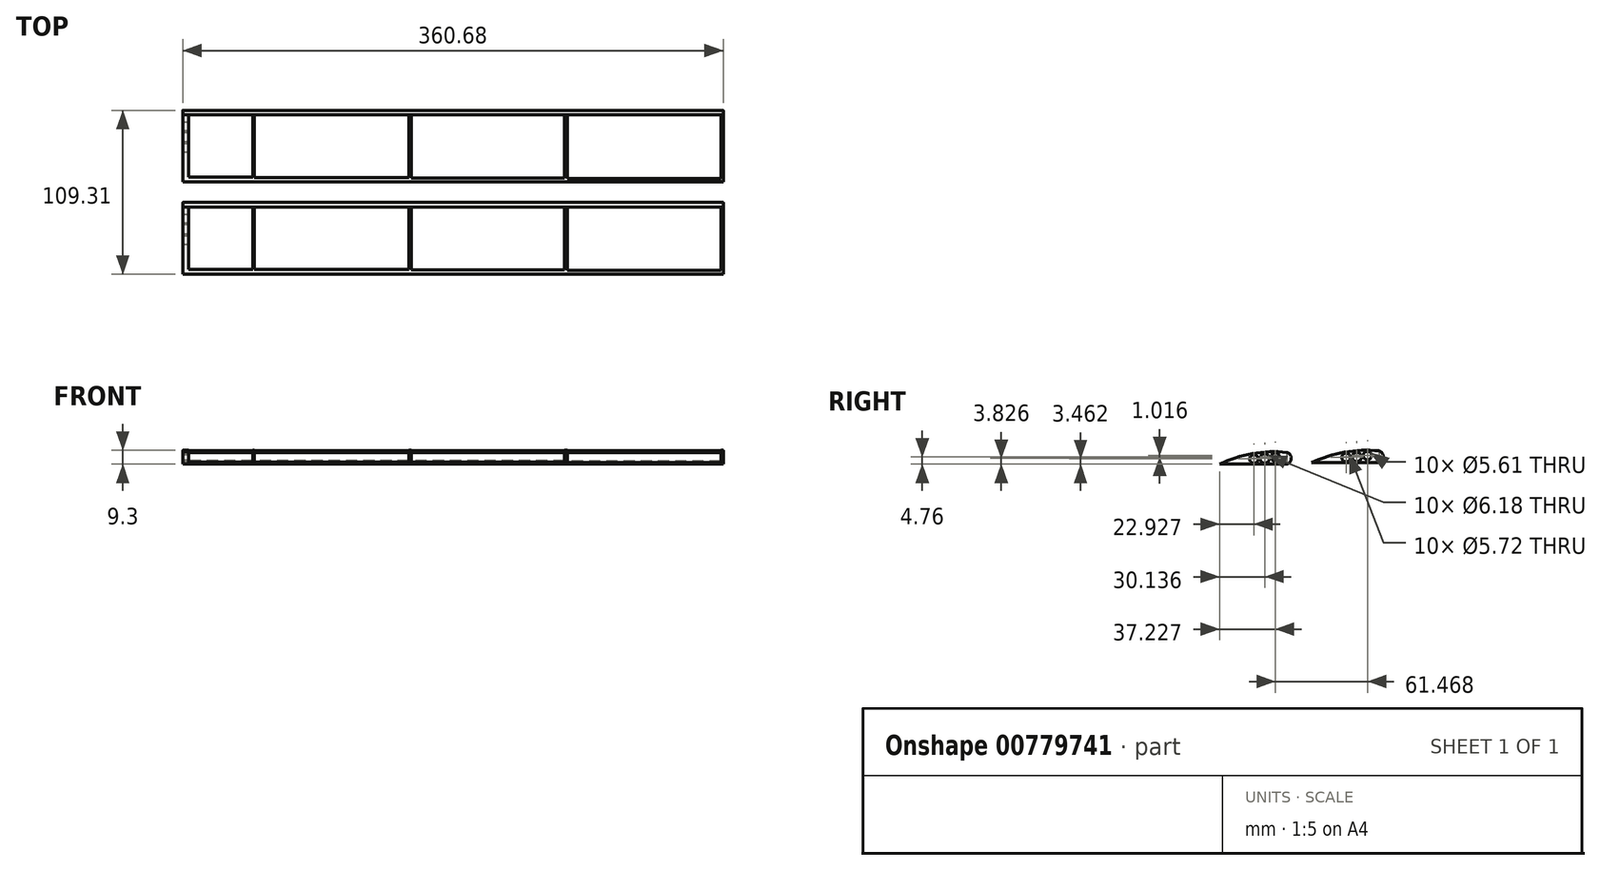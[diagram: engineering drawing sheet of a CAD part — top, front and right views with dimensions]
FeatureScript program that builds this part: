
annotation { "Feature Type Name" : "Feature", "Feature Type Description" : "" }
export const myFeature = defineFeature(function(context is Context, id is Id, definition is map)
    precondition{}
    {
        {
            var Q0;
            Q0=qCreatedBy(makeId("Right.planeOp"),FACE);
            var sketch = newSketch(context, id + "F0", { "sketchPlane" : qUnion([Q0])});
            skArc(sketch, "E0", {"start": v(0, 0) * mm, "mid": v(3, 3.95) * mm, "end": v(0, 7.9) * mm});
            skArc(sketch, "E1", {"start": v(0, 7.9) * mm, "mid": v(-22.96, 7) * mm, "end": v(-44.85, 0) * mm});
            skLineSegment(sketch, "E2", {"start": v(0, 0) * mm, "end": v(-44.85, 0) * mm});
            skSolve(sketch);
        }
        {
            var Q0;
            Q0 = qSketchRegion(id + "F0", true);
            var Q1;
            Q1 = qSketchRegion(id + "F35AifiYWSmg4aq_1", true);
            extrude(context, id + "F1", {"entities" : qUnion([Q0, Q1]), "depth" : 360.68 * mm, "offsetDistance" : 25.4 * mm});
        }
        {
            var Q0;
            Q0=makeQuery(id+"F1.opExtrude","CAP_FACE",FACE,{"disambiguationData":[OSD([sQuery(id+"F0.wireOp",EDGE,"E0"),sQuery(id+"F0.wireOp",EDGE,"E1"),sQuery(id+"F0.wireOp",EDGE,"E2")])],"isStart":false});
            var sketch = newSketch(context, id + "F2", { "sketchPlane" : qUnion([Q0])});
            skCircle(sketch, "E3", {"center": v(-1.1, 3.95) * mm, "radius": 3.21 * mm});
            skSolve(sketch);
        }
        {
            var Q0;
            Q0 = qSketchRegion(id + "F2", true);
            extrude(context, id + "F3", {"entities" : qUnion([Q0]), "operationType" : NewBodyOperationType.REMOVE, "depth" : 63.75 * mm, "offsetDistance" : 25.4 * mm});
        }
        {
            var Q0;
            Q0=qCreatedBy(makeId("Right.planeOp"),FACE);
            cPlane(context, id + "F4", {"entities" : qUnion([Q0]), "cplaneType" : CPlaneType.OFFSET, "offset" : 728.98 * mm, "width" : 152.4 * mm, "height" : 152.4 * mm});
        }
        {
            var Q0;
            Q0=qCreatedBy(id+"F4.planeOp",FACE);
            var sketch = newSketch(context, id + "F5", { "sketchPlane" : qUnion([Q0])});
            skCircle(sketch, "E4", {"center": v(-7.62, 4.76) * mm, "radius": 2.8 * mm});
            skSolve(sketch);
        }
        {
            var Q0;
            Q0 = qSketchRegion(id + "F5", true);
            extrude(context, id + "F6", {"entities" : qUnion([Q0]), "operationType" : NewBodyOperationType.REMOVE, "oppositeDirection" : true, "depth" : 762 * mm, "offsetDistance" : 25.4 * mm});
        }
        {
            var Q0;
            Q0=qCreatedBy(id+"F4.planeOp",FACE);
            var sketch = newSketch(context, id + "F7", { "sketchPlane" : qUnion([Q0])});
            skCircle(sketch, "E5", {"center": v(-14.71, 3.83) * mm, "radius": 3.09 * mm});
            skSolve(sketch);
        }
        {
            var Q0;
            Q0 = qSketchRegion(id + "F7", true);
            extrude(context, id + "F8", {"entities" : qUnion([Q0]), "operationType" : NewBodyOperationType.REMOVE, "oppositeDirection" : true, "depth" : 780.8 * mm, "offsetDistance" : 25.4 * mm});
        }
        {
            var Q0;
            Q0=qCreatedBy(id+"F4.planeOp",FACE);
            var sketch = newSketch(context, id + "F9", { "sketchPlane" : qUnion([Q0])});
            skCircle(sketch, "E6", {"center": v(-21.92, 3.46) * mm, "radius": 2.86 * mm});
            skSolve(sketch);
        }
        {
            var Q0;
            Q0 = qSketchRegion(id + "F9", true);
            extrude(context, id + "F10", {"entities" : qUnion([Q0]), "operationType" : NewBodyOperationType.REMOVE, "oppositeDirection" : true, "depth" : 1653.54 * mm, "offsetDistance" : 25.4 * mm});
        }
        {
            var Q0;
            Q0=qCreatedBy(makeId("Top.planeOp"),FACE);
            cPlane(context, id + "F11", {"entities" : qUnion([Q0]), "cplaneType" : CPlaneType.OFFSET, "offset" : 200.66 * mm, "oppositeDirection" : true, "width" : 152.4 * mm, "height" : 152.4 * mm});
        }
        {
            var Q0;
            Q0=qCreatedBy(id+"F11.planeOp",FACE);
            var sketch = newSketch(context, id + "F12", { "sketchPlane" : qUnion([Q0])});
            skLineSegment(sketch, "E7.bottom", {"start": v(359.1, 0) * mm, "end": v(256.65, 0) * mm});
            skLineSegment(sketch, "E7.top", {"start": v(359.1, -42.37) * mm, "end": v(256.65, -42.37) * mm});
            skLineSegment(sketch, "E7.left", {"start": v(359.1, 0) * mm, "end": v(359.1, -42.37) * mm});
            skLineSegment(sketch, "E7.right", {"start": v(256.65, 0) * mm, "end": v(256.65, -42.37) * mm});
            skSolve(sketch);
        }
        {
            var Q0;
            Q0 = qSketchRegion(id + "F12", true);
            extrude(context, id + "F13", {"entities" : qUnion([Q0]), "operationType" : NewBodyOperationType.REMOVE, "depth" : 404.1 * mm, "offsetDistance" : 25.4 * mm});
        }
        {
            var Q0;
            Q0=qCreatedBy(id+"F11.planeOp",FACE);
            var sketch = newSketch(context, id + "F14", { "sketchPlane" : qUnion([Q0])});
            skLineSegment(sketch, "E8.bottom", {"start": v(254.84, 0) * mm, "end": v(152.39, 0) * mm});
            skLineSegment(sketch, "E8.top", {"start": v(254.84, -42.03) * mm, "end": v(152.39, -42.03) * mm});
            skLineSegment(sketch, "E8.left", {"start": v(254.84, 0) * mm, "end": v(254.84, -42.03) * mm});
            skLineSegment(sketch, "E8.right", {"start": v(152.39, 0) * mm, "end": v(152.39, -42.03) * mm});
            skSolve(sketch);
        }
        {
            var Q0;
            Q0 = qSketchRegion(id + "F14", true);
            extrude(context, id + "F15", {"entities" : qUnion([Q0]), "operationType" : NewBodyOperationType.REMOVE, "depth" : 473.2 * mm, "offsetDistance" : 25.4 * mm});
        }
        {
            var Q0;
            Q0=qCreatedBy(id+"F11.planeOp",FACE);
            var sketch = newSketch(context, id + "F16", { "sketchPlane" : qUnion([Q0])});
            skLineSegment(sketch, "E9.bottom", {"start": v(150.92, 0) * mm, "end": v(47.9, 0) * mm});
            skLineSegment(sketch, "E9.top", {"start": v(150.92, -41.71) * mm, "end": v(47.9, -41.71) * mm});
            skLineSegment(sketch, "E9.left", {"start": v(150.92, 0) * mm, "end": v(150.92, -41.71) * mm});
            skLineSegment(sketch, "E9.right", {"start": v(47.9, 0) * mm, "end": v(47.9, -41.71) * mm});
            skSolve(sketch);
        }
        {
            var Q0;
            Q0 = qSketchRegion(id + "F16", true);
            extrude(context, id + "F17", {"entities" : qUnion([Q0]), "operationType" : NewBodyOperationType.REMOVE, "depth" : 452.37 * mm, "offsetDistance" : 25.4 * mm});
        }
        {
            var Q0;
            Q0=qCreatedBy(id+"F11.planeOp",FACE);
            var sketch = newSketch(context, id + "F18", { "sketchPlane" : qUnion([Q0])});
            skLineSegment(sketch, "E10.bottom", {"start": v(46.63, 0) * mm, "end": v(4.03, 0) * mm});
            skLineSegment(sketch, "E10.top", {"start": v(46.63, -41.67) * mm, "end": v(4.03, -41.67) * mm});
            skLineSegment(sketch, "E10.left", {"start": v(46.63, 0) * mm, "end": v(46.63, -41.67) * mm});
            skLineSegment(sketch, "E10.right", {"start": v(4.03, 0) * mm, "end": v(4.03, -41.67) * mm});
            skSolve(sketch);
        }
        {
            var Q0;
            Q0 = qSketchRegion(id + "F18", true);
            extrude(context, id + "F19", {"entities" : qUnion([Q0]), "operationType" : NewBodyOperationType.REMOVE, "depth" : 565.4 * mm, "offsetDistance" : 25.4 * mm});
        }
        {
            var Q0;
            Q0=makeQuery(id+"F1.opExtrude","SWEPT_BODY",BODY,{"disambiguationData":[OSD([sQuery(id+"F0.wireOp",EDGE,"E0"),sQuery(id+"F0.wireOp",EDGE,"E1"),sQuery(id+"F0.wireOp",EDGE,"E2")])]});
            transform(context, id + "F20", {"entities" : qUnion([Q0]), "transformType" : TransformType.TRANSLATION_3D, "dx" : 0 * mm, "dy" : 61.47 * mm, "dz" : 1.02 * mm, "makeCopy" : true});
        }
    });
